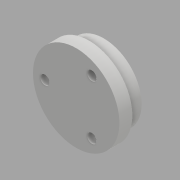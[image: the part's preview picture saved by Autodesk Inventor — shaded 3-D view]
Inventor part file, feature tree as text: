
AUTODESK INVENTOR PART (.ipt)
format: ipt  version: 2017 (Build 210142000, 142)  size: 100,352 bytes
history: native  units: mm
features: sketch x3, extrude x2, hole x1
ambient origin geometry x8: Origin, YZ Plane, XZ Plane, XY Plane, X Axis, Y Axis, Z Axis, Center Point
bodies: Solid1 (feature_tree)
feature tree (6):
  extrude  "Extrusion1"  Depth=6.0mm TaperAngle=0.0deg
  extrude  "Extrusion2"  Depth=6.8mm TaperAngle=0.0deg
  hole  "Hole1"  [1 undecoded]
  sketch  "Sketch1"  dims[d0=40.0mm d1=6.0mm d2=0.0mm]
  sketch  "Sketch2"  dims[d3=35.0mm d4=6.8mm d5=0.0mm]
  sketch  "Sketch3"  dims[d6=29.0mm d7=30.0mm d9=360.0deg d11=4.3mm d12=6.0mm d13=4.0mm d14=2.0mm d15=90.0deg d16=8.0mm d17=20.594885mm]
note: 1 required parameter value undecoded (feature->parameter linkage not recoverable at this tier; creation-order binding heuristic only, values carry confidence <= 0.55)
